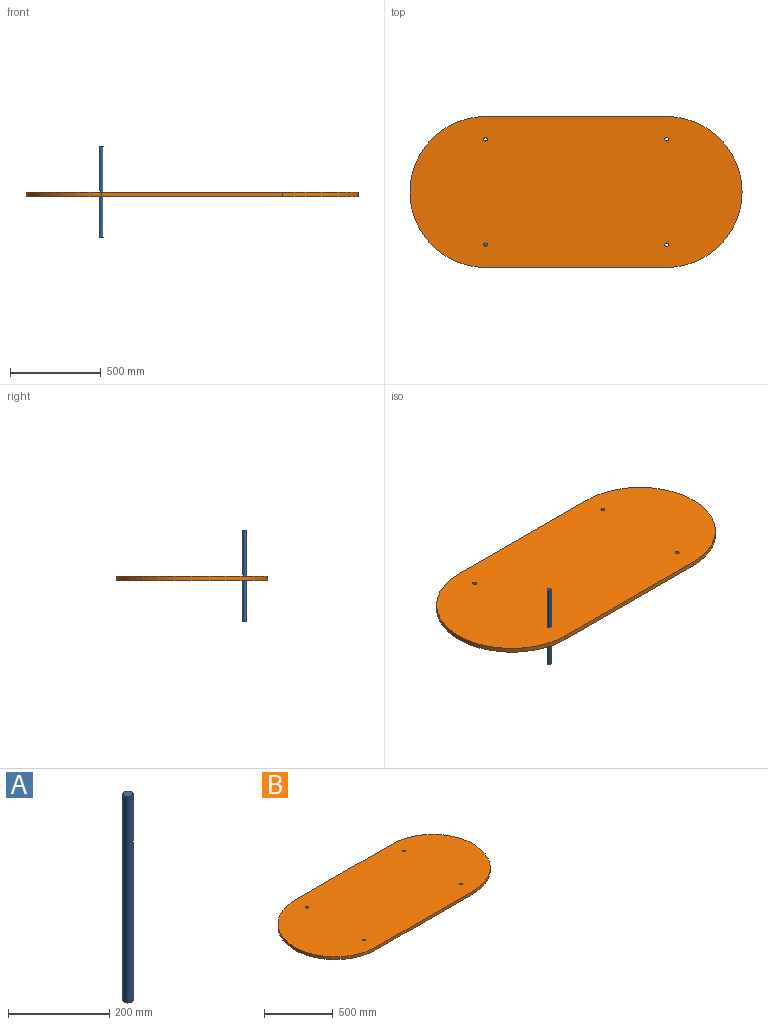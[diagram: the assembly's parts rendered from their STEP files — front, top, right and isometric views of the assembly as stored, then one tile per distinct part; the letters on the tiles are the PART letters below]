
ASSEMBLY  parts=2 mates=1
PART A: 3 faces, bbox 20x20x500 mm
  f0: plane 20x20mm, normal (0,0,-1), area 314.2mm2, adj f1
  f1: cylinder r=10mm len=500mm, axis (0,0,-1), area 31415.9mm2, adj f0,f2
  f2: plane 20x20mm, normal (0,0,1), area 314.2mm2, adj f1
PART B: 10 faces, bbox 1833.1x833.1x25 mm
  f0: plane 1000x25mm, normal (0,-1,0), area 25000mm2, adj f1,f7,f8,f9
  f1: cylinder r=416.54mm len=833.09mm, axis (0,0,-1), area 32715.3mm2, adj f0,f2,f8,f9
  f2: plane 1000x25mm, normal (0,1,0), area 25000mm2, adj f1,f7,f8,f9
  f3: cylinder r=10mm len=25mm, axis (0,0,-1), area 1570.8mm2, adj f8,f9
  f4: cylinder r=10mm len=25mm, axis (0,0,-1), area 1570.8mm2, adj f8,f9
  f5: cylinder r=10mm len=25mm, axis (0,0,-1), area 1570.8mm2, adj f8,f9
  f6: cylinder r=10mm len=25mm, axis (0,0,-1), area 1570.8mm2, adj f8,f9
  f7: cylinder r=416.54mm len=833.09mm, axis (0,0,-1), area 32715.3mm2, adj f0,f2,f8,f9
  f8: plane 1833.09x833.09mm, normal (0,0,1), area 1376928.4mm2, adj f0,f1,f2,f3,f4,f5,f6,f7
  f9: plane 1833.09x833.09mm, normal (0,0,-1), area 1376928.4mm2, adj f0,f1,f2,f3,f4,f5,f6,f7
PLACE A t=(-309.21,-291.54,-265.78)mm
PLACE B at identity
MATE revolute A.f1 <-> B.f6  axis (0,0,-1) through (-500,-291.54,25)mm
